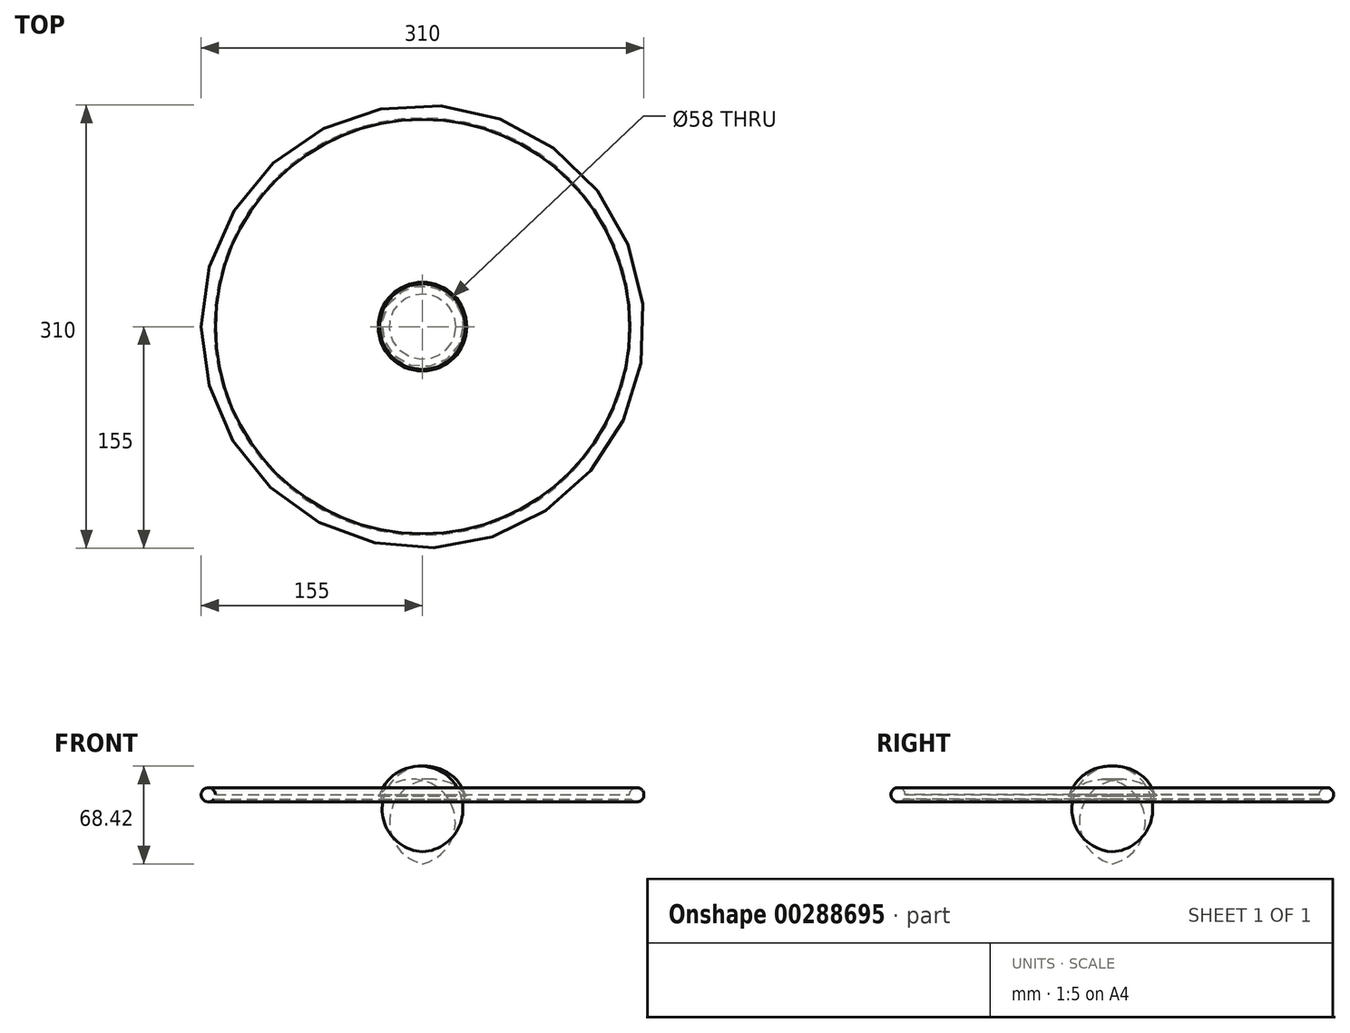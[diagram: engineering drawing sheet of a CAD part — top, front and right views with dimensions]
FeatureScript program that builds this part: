
annotation { "Feature Type Name" : "Feature", "Feature Type Description" : "" }
export const myFeature = defineFeature(function(context is Context, id is Id, definition is map)
    precondition{}
    {
        {
            var Q0;
            Q0=qCreatedBy(makeId("Front.planeOp"),FACE);
            var sketch = newSketch(context, id + "F0", { "sketchPlane" : qUnion([Q0])});
            skLineSegment(sketch, "E0", {"start": v(0, 0) * mm, "end": v(30, 0) * mm});
            skCircle(sketch, "E1", {"center": v(150, 0) * mm, "radius": 5 * mm});
            skLineSegment(sketch, "E2.0", {"start": v(0, -3) * mm, "end": v(150, -3) * mm});
            skLineSegment(sketch, "E3", {"start": v(0, 0) * mm, "end": v(0, -3) * mm});
            skLineSegment(sketch, "E4", {"start": v(30, 0) * mm, "end": v(30, -1) * mm});
            skLineSegment(sketch, "E5", {"start": v(0, 0) * mm, "end": v(0, 20) * mm});
            skArc(sketch, "E6", {"start": v(30, 0) * mm, "mid": v(18.34, 15) * mm, "end": v(0, 20) * mm});
            skArc(sketch, "E7", {"start": v(30, 0) * mm, "mid": v(16.42, 9.27) * mm, "end": v(0, 10) * mm});
            skLineSegment(sketch, "E8", {"start": v(29, 0) * mm, "end": v(29, -3) * mm});
            skArc(sketch, "E9.trimOffspring", {"start": v(29, 0) * mm, "mid": v(30, -1) * mm, "end": v(31, 0) * mm});
            skPoint(sketch, "E10.orphan", {"position": v(30, -3) * mm});
            skLineSegment(sketch, "E11.trimOffspring", {"start": v(31, 0) * mm, "end": v(150, 0) * mm});
            skSolve(sketch);
        }
        {
            var Q0;
            {var subQ0=sQuery(id+"F0.wireOp",EDGE,"E6");Q0=makeQuery(id+"F0.imprint","IMPRINT",FACE,{"disambiguationData":[TD([[makeQuery(id+"F0.imprint","IMPRINT",EDGE,{"derivedFrom":subQ0}),1.0]])]});}
            var Q1;
            {var subQ2=sQuery(id+"F0.wireOp",EDGE,"E8");Q1=makeQuery(id+"F0.imprint","IMPRINT",FACE,{"disambiguationData":[TD([[makeQuery(id+"F0.imprint","IMPRINT",EDGE,{"derivedFrom":subQ2}),1.0]])]});}
            var Q2;
            {var subQ0=sQuery(id+"F0.wireOp",EDGE,"E1");var subQ1=makeQuery(id+"F0.imprint","INTERSECT",VERTEX,{"derivedFrom":[subQ0,sQuery(id+"F0.wireOp",EDGE,"E2.0")]});Q2=makeQuery(id+"F0.imprint","IMPRINT",FACE,{"disambiguationData":[TD([[makeQuery(id+"F0.imprint","IMPRINT",EDGE,{"disambiguationData":[TD([[subQ1,1.0]])],"derivedFrom":subQ0}),1.0]])]});}
            var Q3;
            Q3=sQuery(id+"F0.wireOp",EDGE,"E5");
            revolve(context, id + "F1", {"entities" : qUnion([Q0, Q1, Q2]), "axis" : qUnion([Q3]), "revolveType" : RevolveType.FULL});
        }
    });
